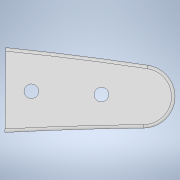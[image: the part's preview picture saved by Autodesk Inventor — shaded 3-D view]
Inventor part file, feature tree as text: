
AUTODESK INVENTOR PART (.ipt)
format: ipt  version: 2020.3 (Build 243373000, 373)  size: 209,920 bytes
history: native  units: mm
features: sketch x1, extrude x1, shell x1, hole x1, fillet x1
ambient origin geometry x8: Origin, YZ Plane, XZ Plane, XY Plane, X Axis, Y Axis, Z Axis, Center Point
bodies: Body1 (feature_tree)
feature tree (5):
  sketch  "Sketch1"  dims[d4=6.0mm d5=24.6mm d6=12.4mm d7=6.0mm d15=7.0mm d17=9.0mm d21=20.0mm d23=80.0mm d24=20.0mm d29=29.670597mm d30=6.0mm d31=10.0mm d43=4.0mm d44=3.0mm d45=4.0mm d50=13.0mm d51=12.0mm d52=22.68928mm d89=6.8mm d90=28.4mm d107=420.0mm d108=4.0mm d109=4.0mm d114=1.0mm d115=1.0mm d116=8.0mm d117=0.0mm d118=1.0mm d119=2.1mm d120=6.0mm d121=4.0mm d122=2.0mm d123=90.0deg d124=8.0mm d125=20.594885mm d126=0.5mm]
  extrude  "Extrusion4"  Depth=0.5mm
  shell  "Shell1"  Thickness=12.4mm
  hole  "Hole6"  [1 undecoded]
  fillet  "Fillet12"  Radius=7.0mm
note: 1 required parameter value undecoded (feature->parameter linkage not recoverable at this tier; creation-order binding heuristic only, values carry confidence <= 0.55)
